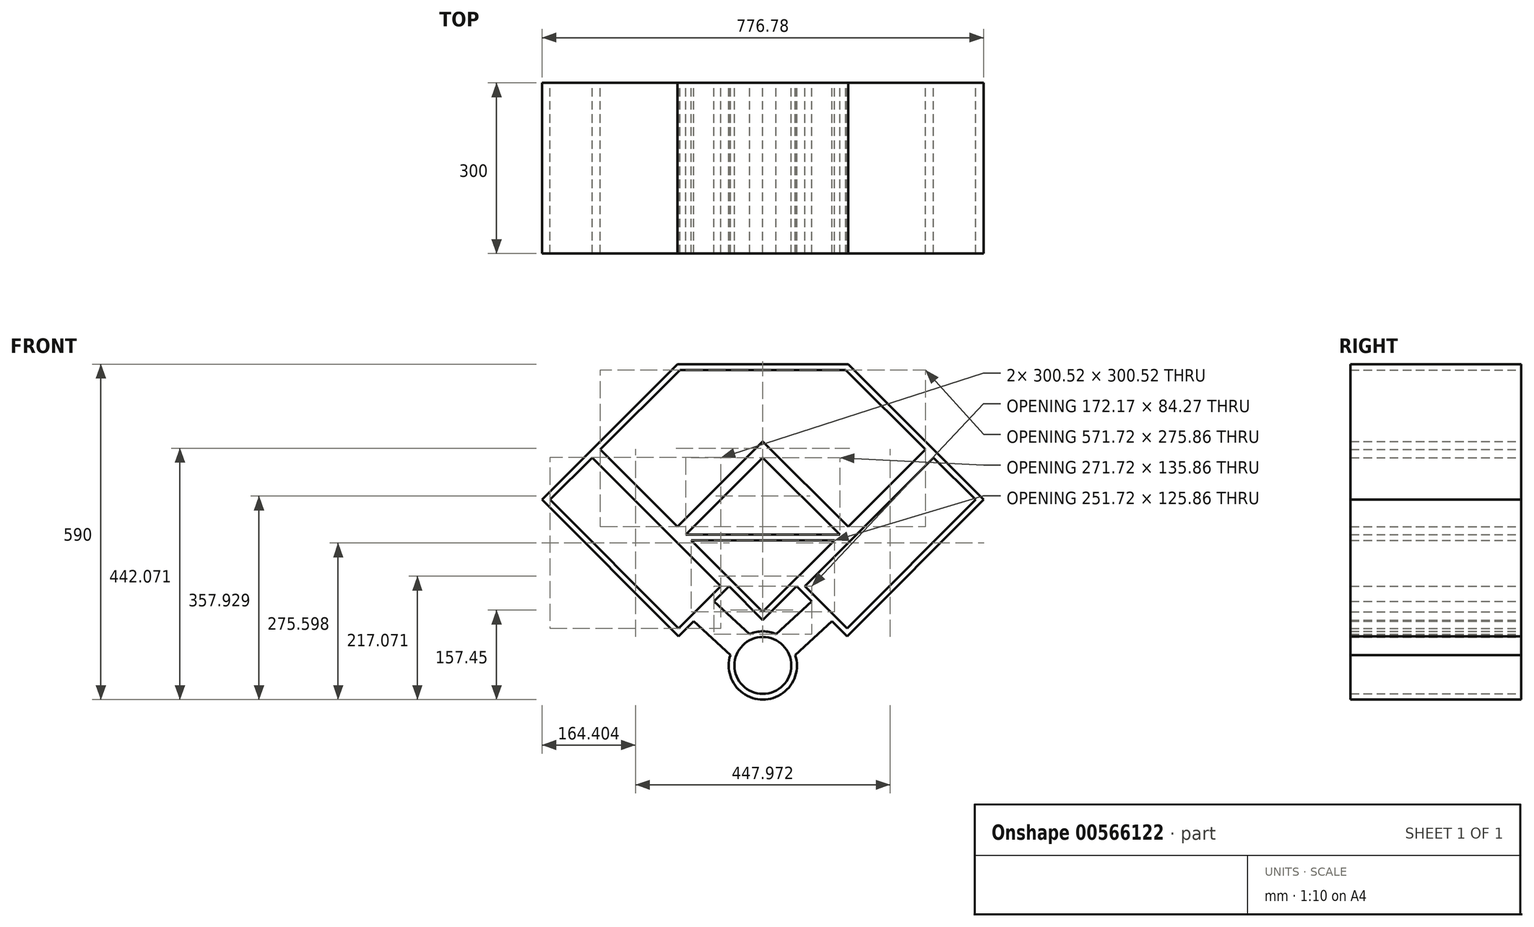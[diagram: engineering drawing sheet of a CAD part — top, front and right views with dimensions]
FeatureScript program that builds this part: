
annotation { "Feature Type Name" : "Feature", "Feature Type Description" : "" }
export const myFeature = defineFeature(function(context is Context, id is Id, definition is map)
    precondition{}
    {
        {
            var Q0;
            Q0=qCreatedBy(makeId("Front.planeOp"),FACE);
            var sketch = newSketch(context, id + "F0", { "sketchPlane" : qUnion([Q0])});
            skLineSegment(sketch, "E0", {"start": v(-300, 0) * mm, "end": v(-150, 150) * mm});
            skLineSegment(sketch, "E1", {"start": v(150, 150) * mm, "end": v(300, 0) * mm});
            skLineSegment(sketch, "E2", {"start": v(150, -150) * mm, "end": v(0, -300) * mm});
            skLineSegment(sketch, "E3", {"start": v(0, -300) * mm, "end": v(-150, -150) * mm});
            skPoint(sketch, "E4.endSnap0", {"position": v(150, 150) * mm});
            skLineSegment(sketch, "E5.0", {"start": v(0, -285.86) * mm, "end": v(-135.86, -150) * mm});
            skLineSegment(sketch, "E5.1", {"start": v(135.86, -150) * mm, "end": v(0, -285.86) * mm});
            skLineSegment(sketch, "E6.0", {"start": v(-67.93, -82.07) * mm, "end": v(-135.86, -150) * mm});
            skLineSegment(sketch, "E6.1", {"start": v(-67.93, -82.07) * mm, "end": v(0, -14.14) * mm});
            skLineSegment(sketch, "E6.2", {"start": v(67.93, -82.07) * mm, "end": v(0, -14.14) * mm});
            skLineSegment(sketch, "E6.3", {"start": v(67.93, -82.07) * mm, "end": v(135.86, -150) * mm});
            skLineSegment(sketch, "E7", {"start": v(-150, -150) * mm, "end": v(0, 0) * mm});
            skLineSegment(sketch, "E8", {"start": v(0, 0) * mm, "end": v(150, -150) * mm});
            skLineSegment(sketch, "E9", {"start": v(225, -75) * mm, "end": v(150, -150) * mm});
            skPoint(sketch, "E10.orphan", {"position": v(0, 300) * mm});
            skLineSegment(sketch, "E11", {"start": v(-150, 150) * mm, "end": v(150, 150) * mm});
            skLineSegment(sketch, "E12.0", {"start": v(-150, -135.86) * mm, "end": v(-285.86, 0) * mm});
            skLineSegment(sketch, "E12.1", {"start": v(-285.86, 0) * mm, "end": v(-145.86, 140) * mm});
            skLineSegment(sketch, "E12.2", {"start": v(-150, -135.86) * mm, "end": v(0, 14.14) * mm});
            skLineSegment(sketch, "E12.3", {"start": v(-145.86, 140) * mm, "end": v(145.86, 140) * mm});
            skLineSegment(sketch, "E12.4", {"start": v(0, 14.14) * mm, "end": v(150, -135.86) * mm});
            skLineSegment(sketch, "E12.5", {"start": v(217.93, -67.93) * mm, "end": v(150, -135.86) * mm});
            skLineSegment(sketch, "E12.6", {"start": v(285.86, 0) * mm, "end": v(217.93, -67.93) * mm});
            skLineSegment(sketch, "E12.7", {"start": v(145.86, 140) * mm, "end": v(285.86, 0) * mm});
            skLineSegment(sketch, "E13", {"start": v(-300, 0) * mm, "end": v(-388.39, -88.39) * mm});
            skLineSegment(sketch, "E14", {"start": v(-388.39, -88.39) * mm, "end": v(-147.97, -328.8) * mm});
            skLineSegment(sketch, "E15", {"start": v(-147.97, -328.8) * mm, "end": v(-59.58, -240.42) * mm});
            skLineSegment(sketch, "E16.0", {"start": v(-300, -14.14) * mm, "end": v(-73.73, -240.42) * mm});
            skLineSegment(sketch, "E16.1", {"start": v(-300, -14.14) * mm, "end": v(-374.25, -88.39) * mm});
            skLineSegment(sketch, "E16.2", {"start": v(-374.25, -88.39) * mm, "end": v(-147.97, -314.66) * mm});
            skLineSegment(sketch, "E16.3", {"start": v(-147.97, -314.66) * mm, "end": v(-73.73, -240.42) * mm});
            skLineSegment(sketch, "E17", {"start": v(-300, 0) * mm, "end": v(-150, -150) * mm});
            skLineSegment(sketch, "E18", {"start": v(300, 0) * mm, "end": v(388.39, -88.39) * mm});
            skLineSegment(sketch, "E19", {"start": v(388.39, -88.39) * mm, "end": v(147.97, -328.8) * mm});
            skLineSegment(sketch, "E20", {"start": v(147.97, -328.8) * mm, "end": v(59.58, -240.42) * mm});
            skLineSegment(sketch, "E21.0", {"start": v(73.73, -240.42) * mm, "end": v(300, -14.14) * mm});
            skLineSegment(sketch, "E21.1", {"start": v(147.97, -314.66) * mm, "end": v(73.73, -240.42) * mm});
            skLineSegment(sketch, "E21.2", {"start": v(374.25, -88.39) * mm, "end": v(147.97, -314.66) * mm});
            skLineSegment(sketch, "E21.3", {"start": v(300, -14.14) * mm, "end": v(374.25, -88.39) * mm});
            skLineSegment(sketch, "E22", {"start": v(300, 0) * mm, "end": v(225, -75) * mm});
            skCircle(sketch, "E23", {"center": v(-150, 0) * mm, "radius": 65 * mm});
            skCircle(sketch, "E24", {"center": v(150, 0) * mm, "radius": 65 * mm});
            skCircle(sketch, "E25", {"center": v(0, -380) * mm, "radius": 50 * mm});
            skLineSegment(sketch, "E26", {"start": v(-57.08, -361.5) * mm, "end": v(-121.47, -302.3) * mm});
            skLineSegment(sketch, "E27", {"start": v(-23.24, -324.68) * mm, "end": v(-86.08, -266.92) * mm});
            skLineSegment(sketch, "E28", {"start": v(57.08, -361.5) * mm, "end": v(121.47, -302.3) * mm});
            skLineSegment(sketch, "E29", {"start": v(23.24, -324.68) * mm, "end": v(86.08, -266.92) * mm});
            skPoint(sketch, "E30.end.orphan", {"position": v(-103.78, -284.61) * mm});
            skCircle(sketch, "E31.0", {"center": v(0, -380) * mm, "radius": 60 * mm});
            skLineSegment(sketch, "E32", {"start": v(-135.86, -150) * mm, "end": v(135.86, -150) * mm});
            skLineSegment(sketch, "E33.0", {"start": v(-125.86, -160) * mm, "end": v(125.86, -160) * mm});
            skSolve(sketch);
        }
        {
            var Q0;
            Q0 = qSketchRegion(id + "F0", true);
            var Q1;
            {var subQ0=sQuery(id+"F0.wireOp",EDGE,"E6.0");Q1=makeQuery(id+"F0.imprint","IMPRINT",FACE,{"disambiguationData":[TD([[makeQuery(id+"F0.imprint","IMPRINT",EDGE,{"derivedFrom":subQ0}),-1.0]])]});}
            var Q2;
            {var subQ0=sQuery(id+"F0.wireOp",EDGE,"E32");Q2=makeQuery(id+"F0.imprint","IMPRINT",FACE,{"disambiguationData":[TD([[makeQuery(id+"F0.imprint","IMPRINT",EDGE,{"derivedFrom":subQ0}),-1.0]])]});}
            extrude(context, id + "F1", {"entities" : qUnion([Q0, Q1, Q2]), "depth" : 300 * mm, "offsetDistance" : 25 * mm});
        }
    });
